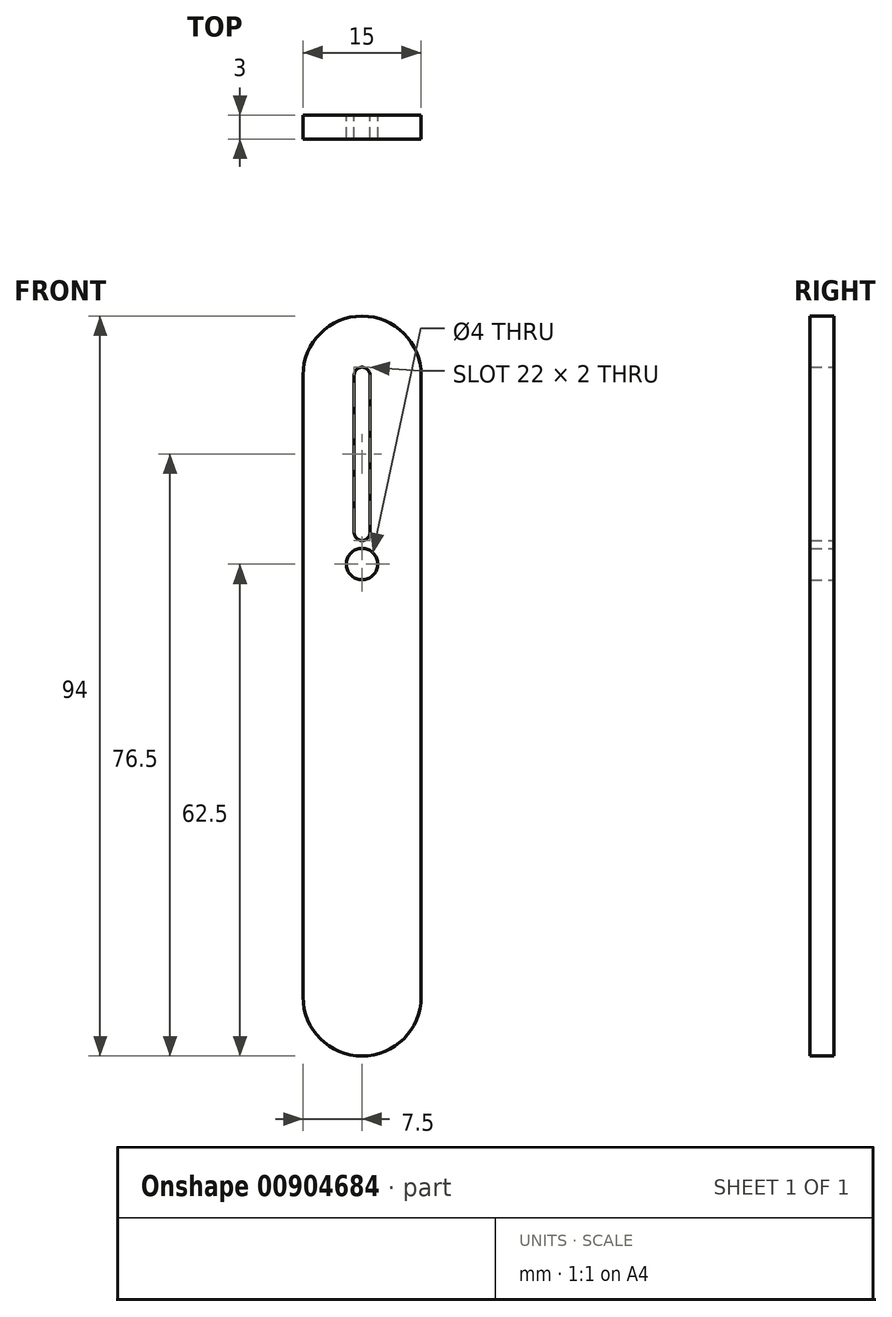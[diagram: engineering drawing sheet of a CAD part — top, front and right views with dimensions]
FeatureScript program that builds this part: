
annotation { "Feature Type Name" : "Feature", "Feature Type Description" : "" }
export const myFeature = defineFeature(function(context is Context, id is Id, definition is map)
    precondition{}
    {
        {
            var Q0;
            Q0=qCreatedBy(makeId("Front.planeOp"),FACE);
            var sketch = newSketch(context, id + "F0", { "sketchPlane" : qUnion([Q0])});
            skArc(sketch, "E0", {"start": v(-7.5, -55) * mm, "mid": v(0, -62.5) * mm, "end": v(7.5, -55) * mm});
            skArc(sketch, "E1", {"start": v(7.5, 24) * mm, "mid": v(0, 31.5) * mm, "end": v(-7.5, 24) * mm});
            skLineSegment(sketch, "E2", {"start": v(-7.5, 24) * mm, "end": v(-7.5, -55) * mm});
            skLineSegment(sketch, "E3.MirrorCS", {"start": v(7.5, 24) * mm, "end": v(7.5, -55) * mm});
            skArc(sketch, "E4", {"start": v(1, 24) * mm, "mid": v(0, 25) * mm, "end": v(-1, 24) * mm});
            skArc(sketch, "E5", {"start": v(-1, 4) * mm, "mid": v(0, 3) * mm, "end": v(1, 4) * mm});
            skCircle(sketch, "E6", {"center": v(0, 0) * mm, "radius": 2 * mm});
            skLineSegment(sketch, "E7", {"start": v(-1, 24) * mm, "end": v(-1, 4) * mm});
            skLineSegment(sketch, "E8", {"start": v(1, 24) * mm, "end": v(1, 4) * mm});
            skSolve(sketch);
        }
        {
            var Q0;
            Q0=makeQuery(id+"F0.imprint","IMPRINT",FACE,{"disambiguationData":[TD([[makeQuery(id+"F0.imprint","IMPRINT",EDGE,{"derivedFrom":sQuery(id+"F0.wireOp",EDGE,"E0")}),1.0]])]});
            extrude(context, id + "F1", {"entities" : qUnion([Q0]), "depth" : 3 * mm, "offsetDistance" : 25 * mm});
        }
    });
